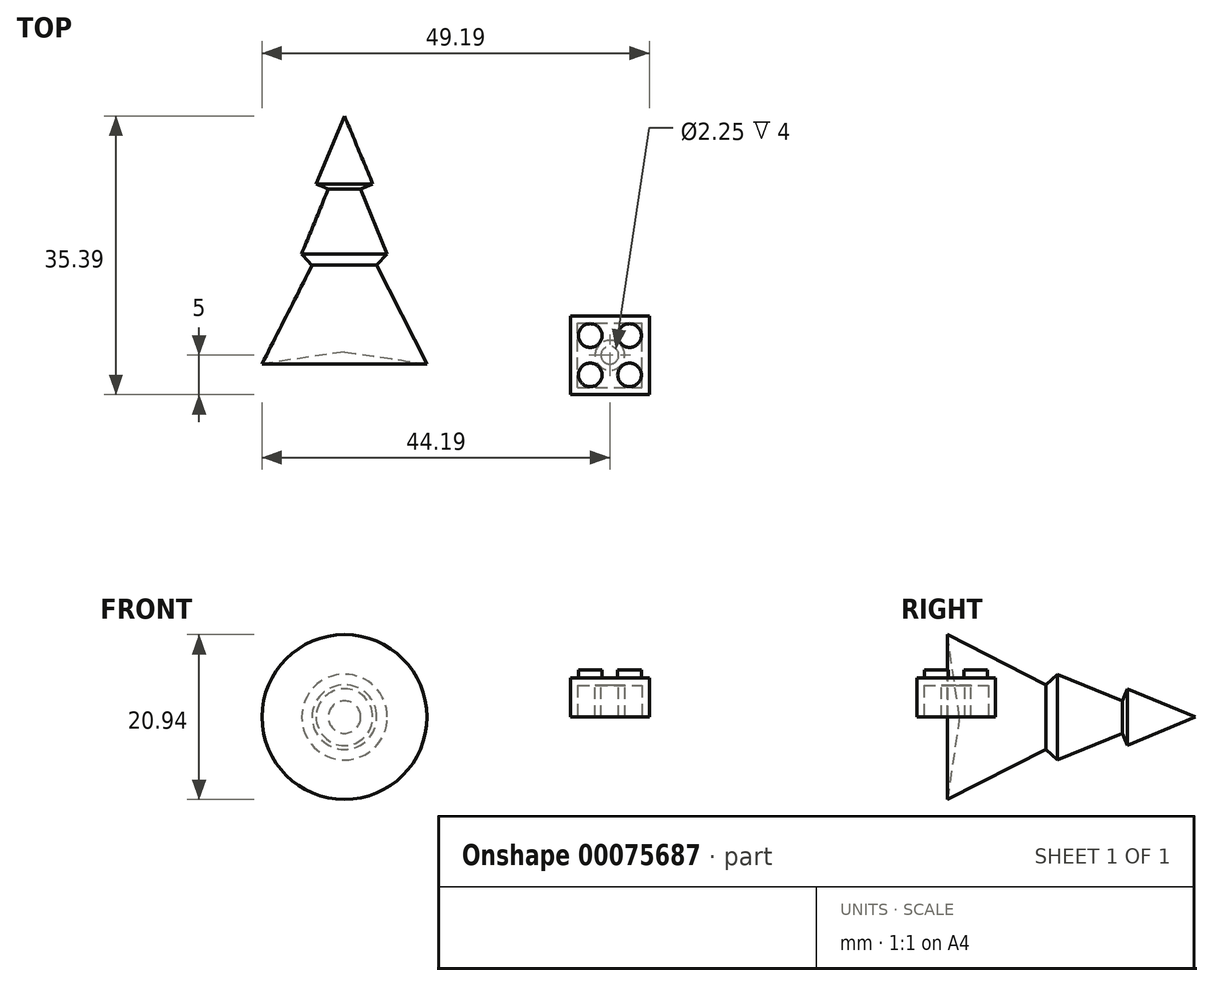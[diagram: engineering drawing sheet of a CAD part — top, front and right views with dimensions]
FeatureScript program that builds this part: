
annotation { "Feature Type Name" : "Feature", "Feature Type Description" : "" }
export const myFeature = defineFeature(function(context is Context, id is Id, definition is map)
    precondition{}
    {
        {
            var Q0;
            Q0=qCreatedBy(makeId("Top.planeOp"),FACE);
            var sketch = newSketch(context, id + "F0", { "sketchPlane" : qUnion([Q0])});
            skLineSegment(sketch, "E0.bottom", {"start": v(0, 0) * mm, "end": v(10, 0) * mm});
            skLineSegment(sketch, "E0.top", {"start": v(0, 10) * mm, "end": v(10, 10) * mm});
            skLineSegment(sketch, "E0.left", {"start": v(0, 0) * mm, "end": v(0, 10) * mm});
            skLineSegment(sketch, "E0.right", {"start": v(10, 0) * mm, "end": v(10, 10) * mm});
            skSolve(sketch);
        }
        {
            var Q0;
            Q0 = qSketchRegion(id + "F0", true);
            extrude(context, id + "F1", {"entities" : qUnion([Q0]), "depth" : 5 * mm});
        }
        {
            var Q0;
            Q0=makeQuery(id+"F1.opExtrude","CAP_FACE",FACE,{"disambiguationData":[OSD([sQuery(id+"F0.wireOp",EDGE,"E0.bottom"),sQuery(id+"F0.wireOp",EDGE,"E0.top"),sQuery(id+"F0.wireOp",EDGE,"E0.left"),sQuery(id+"F0.wireOp",EDGE,"E0.right")])],"isStart":false});
            var sketch = newSketch(context, id + "F2", { "sketchPlane" : qUnion([Q0])});
            skCircle(sketch, "E1", {"center": v(2.5, 7.5) * mm, "radius": 1.5 * mm});
            skCircle(sketch, "E2", {"center": v(7.5, 7.5) * mm, "radius": 1.5 * mm});
            skCircle(sketch, "E3", {"center": v(2.5, 2.5) * mm, "radius": 1.5 * mm});
            skCircle(sketch, "E4", {"center": v(7.5, 2.5) * mm, "radius": 1.5 * mm});
            skSolve(sketch);
        }
        {
            var Q0;
            Q0=makeQuery(id+"F2.imprint","IMPRINT",FACE,{"disambiguationData":[TD([[makeQuery(id+"F2.imprint","IMPRINT",EDGE,{"derivedFrom":sQuery(id+"F2.wireOp",EDGE,"E1")}),1.0]])]});
            var Q1;
            Q1=makeQuery(id+"F2.imprint","IMPRINT",FACE,{"disambiguationData":[TD([[makeQuery(id+"F2.imprint","IMPRINT",EDGE,{"derivedFrom":sQuery(id+"F2.wireOp",EDGE,"E3")}),1.0]])]});
            var Q2;
            Q2=makeQuery(id+"F2.imprint","IMPRINT",FACE,{"disambiguationData":[TD([[makeQuery(id+"F2.imprint","IMPRINT",EDGE,{"derivedFrom":sQuery(id+"F2.wireOp",EDGE,"E4")}),1.0]])]});
            var Q3;
            Q3=makeQuery(id+"F2.imprint","IMPRINT",FACE,{"disambiguationData":[TD([[makeQuery(id+"F2.imprint","IMPRINT",EDGE,{"derivedFrom":sQuery(id+"F2.wireOp",EDGE,"E2")}),1.0]])]});
            extrude(context, id + "F3", {"entities" : qUnion([Q0, Q1, Q2, Q3]), "operationType" : NewBodyOperationType.ADD, "depth" : 1 * mm});
        }
        {
            var Q0;
            Q0=qCreatedBy(makeId("Top.planeOp"),FACE);
            var sketch = newSketch(context, id + "F4", { "sketchPlane" : qUnion([Q0])});
            skLineSegment(sketch, "E5.bottom", {"start": v(0.9, 0.9) * mm, "end": v(9.1, 0.9) * mm});
            skLineSegment(sketch, "E5.top", {"start": v(0.9, 9.1) * mm, "end": v(9.1, 9.1) * mm});
            skLineSegment(sketch, "E5.left", {"start": v(0.9, 0.9) * mm, "end": v(0.9, 9.1) * mm});
            skLineSegment(sketch, "E5.right", {"start": v(9.1, 0.9) * mm, "end": v(9.1, 9.1) * mm});
            skSolve(sketch);
        }
        {
            var Q0;
            Q0=makeQuery(id+"F4.imprint","IMPRINT",FACE,{"disambiguationData":[TD([[makeQuery(id+"F4.imprint","IMPRINT",EDGE,{"derivedFrom":sQuery(id+"F4.wireOp",EDGE,"E5.bottom")}),1.0]])]});
            extrude(context, id + "F5", {"entities" : qUnion([Q0]), "operationType" : NewBodyOperationType.REMOVE, "depth" : 4 * mm});
        }
        {
            var Q0;
            Q0=makeQuery(id+"F5.boolean.opBoolean","COPY",FACE,{"derivedFrom":makeQuery(id+"F5.opExtrude","CAP_FACE",FACE,{"disambiguationData":[OSD([sQuery(id+"F4.wireOp",EDGE,"E5.bottom"),sQuery(id+"F4.wireOp",EDGE,"E5.top"),sQuery(id+"F4.wireOp",EDGE,"E5.left"),sQuery(id+"F4.wireOp",EDGE,"E5.right")])],"isStart":false})});
            var sketch = newSketch(context, id + "F6", { "sketchPlane" : qUnion([Q0])});
            skCircle(sketch, "E6", {"center": v(5, -5) * mm, "radius": 1.9 * mm});
            skCircle(sketch, "E7", {"center": v(5, -5) * mm, "radius": 1.13 * mm});
            skLineSegment(sketch, "E8", {"start": v(0.9, -5) * mm, "end": v(9.1, -5) * mm, "construction": true});
            skSolve(sketch);
        }
        {
            var Q0;
            Q0=makeQuery(id+"F6.imprint","IMPRINT",FACE,{"disambiguationData":[TD([[makeQuery(id+"F6.imprint","IMPRINT",EDGE,{"derivedFrom":sQuery(id+"F6.wireOp",EDGE,"E6")}),1.0]])]});
            var Q1;
            Q1=makeQuery(id+"F1.opExtrude","CAP_FACE",FACE,{"disambiguationData":[OSD([sQuery(id+"F0.wireOp",EDGE,"E0.bottom"),sQuery(id+"F0.wireOp",EDGE,"E0.top"),sQuery(id+"F0.wireOp",EDGE,"E0.left"),sQuery(id+"F0.wireOp",EDGE,"E0.right")])],"isStart":true});
            extrude(context, id + "F7", {"entities" : qUnion([Q0]), "operationType" : NewBodyOperationType.ADD, "endBound" : BoundingType.UP_TO_SURFACE, "endBoundEntityFace" : qUnion([Q1]), "depth" : 25 * mm});
        }
        {
            var Q0;
            Q0=qCreatedBy(makeId("Top.planeOp"),FACE);
            var sketch = newSketch(context, id + "F8", { "sketchPlane" : qUnion([Q0])});
            skLineSegment(sketch, "E9", {"start": v(-28.72, 5.43) * mm, "end": v(-39.19, 3.9) * mm});
            skLineSegment(sketch, "E10", {"start": v(-32.83, 16.43) * mm, "end": v(-34.15, 17.87) * mm});
            skLineSegment(sketch, "E11", {"start": v(-34.15, 17.87) * mm, "end": v(-30.77, 26.11) * mm});
            skLineSegment(sketch, "E12", {"start": v(-30.77, 26.11) * mm, "end": v(-32.31, 26.76) * mm});
            skLineSegment(sketch, "E13", {"start": v(-32.31, 26.76) * mm, "end": v(-28.72, 35.4) * mm});
            skLineSegment(sketch, "E14", {"start": v(-28.72, 35.4) * mm, "end": v(-28.72, 5.43) * mm});
            skPoint(sketch, "E15", {"position": v(-28.72, 20.4) * mm});
            skLineSegment(sketch, "E16", {"start": v(-39.19, 3.9) * mm, "end": v(-32.83, 16.43) * mm});
            skSolve(sketch);
        }
        {
            var Q0;
            Q0=makeQuery(id+"F8.imprint","IMPRINT",FACE,{"disambiguationData":[TD([[makeQuery(id+"F8.imprint","IMPRINT",EDGE,{"derivedFrom":sQuery(id+"F8.wireOp",EDGE,"E9")}),-1.0]])]});
            var Q1;
            Q1=sQuery(id+"F8.wireOp",EDGE,"E14");
            revolve(context, id + "F9", {"entities" : qUnion([Q0]), "axis" : qUnion([Q1]), "revolveType" : RevolveType.FULL});
        }
    });
